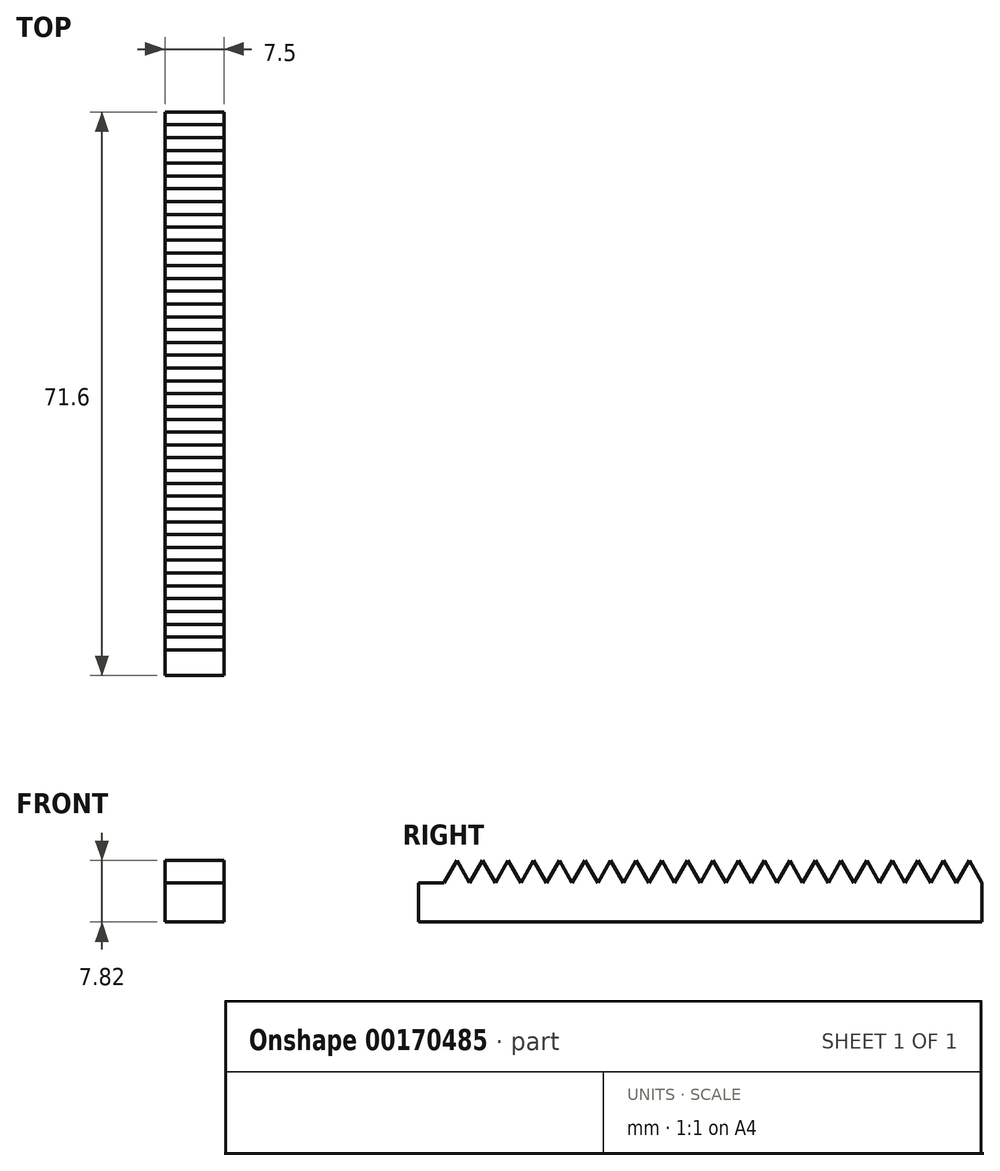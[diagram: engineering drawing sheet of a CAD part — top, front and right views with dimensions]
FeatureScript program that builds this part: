
annotation { "Feature Type Name" : "Feature", "Feature Type Description" : "" }
export const myFeature = defineFeature(function(context is Context, id is Id, definition is map)
    precondition{}
    {
        {
            var Q0;
            Q0=qCreatedBy(makeId("Right.planeOp"),FACE);
            var sketch = newSketch(context, id + "F0", { "sketchPlane" : qUnion([Q0])});
            skLineSegment(sketch, "E0.bottom", {"start": v(35.8, 2.5) * mm, "end": v(-35.8, 2.5) * mm});
            skLineSegment(sketch, "E0.top", {"start": v(35.8, -2.5) * mm, "end": v(-35.8, -2.5) * mm});
            skLineSegment(sketch, "E0.left", {"start": v(35.8, 2.5) * mm, "end": v(35.8, -2.5) * mm});
            skLineSegment(sketch, "E0.right", {"start": v(-35.8, 2.5) * mm, "end": v(-35.8, -2.5) * mm});
            skPoint(sketch, "E0.middle", {"position": v(0, 0) * mm});
            skLineSegment(sketch, "E1", {"start": v(-35.8, 2.5) * mm, "end": v(-32.54, 2.5) * mm});
            skLineSegment(sketch, "E2", {"start": v(-32.54, 2.5) * mm, "end": v(-34.17, 5.32) * mm});
            skLineSegment(sketch, "E3", {"start": v(-34.17, 5.32) * mm, "end": v(-35.8, 2.5) * mm});
            skLineSegment(sketch, "E4.1.0.0", {"start": v(-29.29, 2.5) * mm, "end": v(-30.91, 5.32) * mm});
            skLineSegment(sketch, "E4.1.0.1", {"start": v(-30.91, 5.32) * mm, "end": v(-32.54, 2.5) * mm});
            skLineSegment(sketch, "E4.1.0.2", {"start": v(-32.54, 2.5) * mm, "end": v(-29.29, 2.5) * mm});
            skLineSegment(sketch, "E4.2.0.0", {"start": v(-26.03, 2.5) * mm, "end": v(-27.66, 5.32) * mm});
            skLineSegment(sketch, "E4.2.0.1", {"start": v(-27.66, 5.32) * mm, "end": v(-29.29, 2.5) * mm});
            skLineSegment(sketch, "E4.2.0.2", {"start": v(-29.29, 2.5) * mm, "end": v(-26.03, 2.5) * mm});
            skLineSegment(sketch, "E4.3.0.0", {"start": v(-22.78, 2.5) * mm, "end": v(-24.4, 5.32) * mm});
            skLineSegment(sketch, "E4.3.0.1", {"start": v(-24.4, 5.32) * mm, "end": v(-26.03, 2.5) * mm});
            skLineSegment(sketch, "E4.3.0.2", {"start": v(-26.03, 2.5) * mm, "end": v(-22.78, 2.5) * mm});
            skLineSegment(sketch, "E4.4.0.0", {"start": v(-19.52, 2.5) * mm, "end": v(-21.15, 5.32) * mm});
            skLineSegment(sketch, "E4.4.0.1", {"start": v(-21.15, 5.32) * mm, "end": v(-22.78, 2.5) * mm});
            skLineSegment(sketch, "E4.4.0.2", {"start": v(-22.78, 2.5) * mm, "end": v(-19.52, 2.5) * mm});
            skLineSegment(sketch, "E4.5.0.0", {"start": v(-16.27, 2.5) * mm, "end": v(-17.9, 5.32) * mm});
            skLineSegment(sketch, "E4.5.0.1", {"start": v(-17.9, 5.32) * mm, "end": v(-19.52, 2.5) * mm});
            skLineSegment(sketch, "E4.5.0.2", {"start": v(-19.52, 2.5) * mm, "end": v(-16.27, 2.5) * mm});
            skLineSegment(sketch, "E4.6.0.0", {"start": v(-13.02, 2.5) * mm, "end": v(-14.64, 5.32) * mm});
            skLineSegment(sketch, "E4.6.0.1", {"start": v(-14.64, 5.32) * mm, "end": v(-16.27, 2.5) * mm});
            skLineSegment(sketch, "E4.6.0.2", {"start": v(-16.27, 2.5) * mm, "end": v(-13.02, 2.5) * mm});
            skLineSegment(sketch, "E4.7.0.0", {"start": v(-9.76, 2.5) * mm, "end": v(-11.39, 5.32) * mm});
            skLineSegment(sketch, "E4.7.0.1", {"start": v(-11.39, 5.32) * mm, "end": v(-13.02, 2.5) * mm});
            skLineSegment(sketch, "E4.7.0.2", {"start": v(-13.02, 2.5) * mm, "end": v(-9.76, 2.5) * mm});
            skLineSegment(sketch, "E4.8.0.0", {"start": v(-6.5, 2.5) * mm, "end": v(-8.14, 5.32) * mm});
            skLineSegment(sketch, "E4.8.0.1", {"start": v(-8.14, 5.32) * mm, "end": v(-9.76, 2.5) * mm});
            skLineSegment(sketch, "E4.8.0.2", {"start": v(-9.76, 2.5) * mm, "end": v(-6.5, 2.5) * mm});
            skLineSegment(sketch, "E4.9.0.0", {"start": v(-3.25, 2.5) * mm, "end": v(-4.88, 5.32) * mm});
            skLineSegment(sketch, "E4.9.0.1", {"start": v(-4.88, 5.32) * mm, "end": v(-6.5, 2.5) * mm});
            skLineSegment(sketch, "E4.9.0.2", {"start": v(-6.5, 2.5) * mm, "end": v(-3.25, 2.5) * mm});
            skLineSegment(sketch, "E4.10.0.0", {"start": v(0, 2.5) * mm, "end": v(-1.63, 5.32) * mm});
            skLineSegment(sketch, "E4.10.0.1", {"start": v(-1.63, 5.32) * mm, "end": v(-3.25, 2.5) * mm});
            skLineSegment(sketch, "E4.10.0.2", {"start": v(-3.25, 2.5) * mm, "end": v(0, 2.5) * mm});
            skLineSegment(sketch, "E4.11.0.0", {"start": v(3.25, 2.5) * mm, "end": v(1.63, 5.32) * mm});
            skLineSegment(sketch, "E4.11.0.1", {"start": v(1.63, 5.32) * mm, "end": v(0, 2.5) * mm});
            skLineSegment(sketch, "E4.11.0.2", {"start": v(0, 2.5) * mm, "end": v(3.25, 2.5) * mm});
            skLineSegment(sketch, "E4.12.0.0", {"start": v(6.5, 2.5) * mm, "end": v(4.88, 5.32) * mm});
            skLineSegment(sketch, "E4.12.0.1", {"start": v(4.88, 5.32) * mm, "end": v(3.25, 2.5) * mm});
            skLineSegment(sketch, "E4.12.0.2", {"start": v(3.25, 2.5) * mm, "end": v(6.5, 2.5) * mm});
            skLineSegment(sketch, "E4.13.0.0", {"start": v(9.76, 2.5) * mm, "end": v(8.14, 5.32) * mm});
            skLineSegment(sketch, "E4.13.0.1", {"start": v(8.14, 5.32) * mm, "end": v(6.5, 2.5) * mm});
            skLineSegment(sketch, "E4.13.0.2", {"start": v(6.5, 2.5) * mm, "end": v(9.76, 2.5) * mm});
            skLineSegment(sketch, "E4.14.0.0", {"start": v(13.02, 2.5) * mm, "end": v(11.39, 5.32) * mm});
            skLineSegment(sketch, "E4.14.0.1", {"start": v(11.39, 5.32) * mm, "end": v(9.76, 2.5) * mm});
            skLineSegment(sketch, "E4.14.0.2", {"start": v(9.76, 2.5) * mm, "end": v(13.02, 2.5) * mm});
            skLineSegment(sketch, "E4.15.0.0", {"start": v(16.27, 2.5) * mm, "end": v(14.64, 5.32) * mm});
            skLineSegment(sketch, "E4.15.0.1", {"start": v(14.64, 5.32) * mm, "end": v(13.02, 2.5) * mm});
            skLineSegment(sketch, "E4.15.0.2", {"start": v(13.02, 2.5) * mm, "end": v(16.27, 2.5) * mm});
            skLineSegment(sketch, "E4.16.0.0", {"start": v(19.52, 2.5) * mm, "end": v(17.9, 5.32) * mm});
            skLineSegment(sketch, "E4.16.0.1", {"start": v(17.9, 5.32) * mm, "end": v(16.27, 2.5) * mm});
            skLineSegment(sketch, "E4.16.0.2", {"start": v(16.27, 2.5) * mm, "end": v(19.52, 2.5) * mm});
            skLineSegment(sketch, "E4.17.0.0", {"start": v(22.78, 2.5) * mm, "end": v(21.15, 5.32) * mm});
            skLineSegment(sketch, "E4.17.0.1", {"start": v(21.15, 5.32) * mm, "end": v(19.52, 2.5) * mm});
            skLineSegment(sketch, "E4.17.0.2", {"start": v(19.52, 2.5) * mm, "end": v(22.78, 2.5) * mm});
            skLineSegment(sketch, "E4.18.0.0", {"start": v(26.03, 2.5) * mm, "end": v(24.4, 5.32) * mm});
            skLineSegment(sketch, "E4.18.0.1", {"start": v(24.4, 5.32) * mm, "end": v(22.78, 2.5) * mm});
            skLineSegment(sketch, "E4.18.0.2", {"start": v(22.78, 2.5) * mm, "end": v(26.03, 2.5) * mm});
            skLineSegment(sketch, "E4.19.0.0", {"start": v(29.29, 2.5) * mm, "end": v(27.66, 5.32) * mm});
            skLineSegment(sketch, "E4.19.0.1", {"start": v(27.66, 5.32) * mm, "end": v(26.03, 2.5) * mm});
            skLineSegment(sketch, "E4.19.0.2", {"start": v(26.03, 2.5) * mm, "end": v(29.29, 2.5) * mm});
            skLineSegment(sketch, "E4.20.0.0", {"start": v(32.54, 2.5) * mm, "end": v(30.91, 5.32) * mm});
            skLineSegment(sketch, "E4.20.0.1", {"start": v(30.91, 5.32) * mm, "end": v(29.29, 2.5) * mm});
            skLineSegment(sketch, "E4.20.0.2", {"start": v(29.29, 2.5) * mm, "end": v(32.54, 2.5) * mm});
            skLineSegment(sketch, "E4.21.0.0", {"start": v(35.8, 2.5) * mm, "end": v(34.17, 5.32) * mm});
            skLineSegment(sketch, "E4.21.0.1", {"start": v(34.17, 5.32) * mm, "end": v(32.54, 2.5) * mm});
            skLineSegment(sketch, "E4.21.0.2", {"start": v(32.54, 2.5) * mm, "end": v(35.8, 2.5) * mm});
            skLineSegment(sketch, "E4.direction1", {"start": v(-35.8, 2.5) * mm, "end": v(-32.54, 2.5) * mm, "construction": true});
            skSolve(sketch);
        }
        {
            var Q0;
            Q0=makeQuery(id+"F0.imprint","IMPRINT",FACE,{"disambiguationData":[TD([[makeQuery(id+"F0.imprint","IMPRINT",EDGE,{"derivedFrom":sQuery(id+"F0.wireOp",EDGE,"E0.top")}),-1.0]])]});
            var Q1;
            Q1=makeQuery(id+"F0.imprint","IMPRINT",FACE,{"disambiguationData":[TD([[makeQuery(id+"F0.imprint","IMPRINT",EDGE,{"derivedFrom":sQuery(id+"F0.wireOp",EDGE,"E4.19.0.0")}),1.0]])]});
            var Q2;
            Q2=makeQuery(id+"F0.imprint","IMPRINT",FACE,{"disambiguationData":[TD([[makeQuery(id+"F0.imprint","IMPRINT",EDGE,{"derivedFrom":sQuery(id+"F0.wireOp",EDGE,"E4.20.0.0")}),1.0]])]});
            var Q3;
            Q3=makeQuery(id+"F0.imprint","IMPRINT",FACE,{"disambiguationData":[TD([[makeQuery(id+"F0.imprint","IMPRINT",EDGE,{"derivedFrom":sQuery(id+"F0.wireOp",EDGE,"E4.21.0.0")}),1.0]])]});
            var Q4;
            Q4=makeQuery(id+"F0.imprint","IMPRINT",FACE,{"disambiguationData":[TD([[makeQuery(id+"F0.imprint","IMPRINT",EDGE,{"derivedFrom":sQuery(id+"F0.wireOp",EDGE,"E4.15.0.0")}),1.0]])]});
            var Q5;
            Q5=makeQuery(id+"F0.imprint","IMPRINT",FACE,{"disambiguationData":[TD([[makeQuery(id+"F0.imprint","IMPRINT",EDGE,{"derivedFrom":sQuery(id+"F0.wireOp",EDGE,"E4.13.0.0")}),1.0]])]});
            var Q6;
            Q6=makeQuery(id+"F0.imprint","IMPRINT",FACE,{"disambiguationData":[TD([[makeQuery(id+"F0.imprint","IMPRINT",EDGE,{"derivedFrom":sQuery(id+"F0.wireOp",EDGE,"E4.16.0.0")}),1.0]])]});
            var Q7;
            Q7=makeQuery(id+"F0.imprint","IMPRINT",FACE,{"disambiguationData":[TD([[makeQuery(id+"F0.imprint","IMPRINT",EDGE,{"derivedFrom":sQuery(id+"F0.wireOp",EDGE,"E4.14.0.0")}),1.0]])]});
            var Q8;
            Q8=makeQuery(id+"F0.imprint","IMPRINT",FACE,{"disambiguationData":[TD([[makeQuery(id+"F0.imprint","IMPRINT",EDGE,{"derivedFrom":sQuery(id+"F0.wireOp",EDGE,"E1")}),1.0]])]});
            var Q9;
            Q9=makeQuery(id+"F0.imprint","IMPRINT",FACE,{"disambiguationData":[TD([[makeQuery(id+"F0.imprint","IMPRINT",EDGE,{"derivedFrom":sQuery(id+"F0.wireOp",EDGE,"E4.1.0.0")}),1.0]])]});
            var Q10;
            Q10=makeQuery(id+"F0.imprint","IMPRINT",FACE,{"disambiguationData":[TD([[makeQuery(id+"F0.imprint","IMPRINT",EDGE,{"derivedFrom":sQuery(id+"F0.wireOp",EDGE,"E4.2.0.0")}),1.0]])]});
            var Q11;
            Q11=makeQuery(id+"F0.imprint","IMPRINT",FACE,{"disambiguationData":[TD([[makeQuery(id+"F0.imprint","IMPRINT",EDGE,{"derivedFrom":sQuery(id+"F0.wireOp",EDGE,"E4.3.0.0")}),1.0]])]});
            var Q12;
            Q12=makeQuery(id+"F0.imprint","IMPRINT",FACE,{"disambiguationData":[TD([[makeQuery(id+"F0.imprint","IMPRINT",EDGE,{"derivedFrom":sQuery(id+"F0.wireOp",EDGE,"E4.4.0.0")}),1.0]])]});
            var Q13;
            Q13=makeQuery(id+"F0.imprint","IMPRINT",FACE,{"disambiguationData":[TD([[makeQuery(id+"F0.imprint","IMPRINT",EDGE,{"derivedFrom":sQuery(id+"F0.wireOp",EDGE,"E4.5.0.0")}),1.0]])]});
            var Q14;
            Q14=makeQuery(id+"F0.imprint","IMPRINT",FACE,{"disambiguationData":[TD([[makeQuery(id+"F0.imprint","IMPRINT",EDGE,{"derivedFrom":sQuery(id+"F0.wireOp",EDGE,"E4.6.0.0")}),1.0]])]});
            var Q15;
            Q15=makeQuery(id+"F0.imprint","IMPRINT",FACE,{"disambiguationData":[TD([[makeQuery(id+"F0.imprint","IMPRINT",EDGE,{"derivedFrom":sQuery(id+"F0.wireOp",EDGE,"E4.7.0.0")}),1.0]])]});
            var Q16;
            Q16=makeQuery(id+"F0.imprint","IMPRINT",FACE,{"disambiguationData":[TD([[makeQuery(id+"F0.imprint","IMPRINT",EDGE,{"derivedFrom":sQuery(id+"F0.wireOp",EDGE,"E4.8.0.0")}),1.0]])]});
            var Q17;
            Q17=makeQuery(id+"F0.imprint","IMPRINT",FACE,{"disambiguationData":[TD([[makeQuery(id+"F0.imprint","IMPRINT",EDGE,{"derivedFrom":sQuery(id+"F0.wireOp",EDGE,"E4.9.0.0")}),1.0]])]});
            var Q18;
            Q18=makeQuery(id+"F0.imprint","IMPRINT",FACE,{"disambiguationData":[TD([[makeQuery(id+"F0.imprint","IMPRINT",EDGE,{"derivedFrom":sQuery(id+"F0.wireOp",EDGE,"E4.10.0.0")}),1.0]])]});
            var Q19;
            Q19=makeQuery(id+"F0.imprint","IMPRINT",FACE,{"disambiguationData":[TD([[makeQuery(id+"F0.imprint","IMPRINT",EDGE,{"derivedFrom":sQuery(id+"F0.wireOp",EDGE,"E4.11.0.0")}),1.0]])]});
            var Q20;
            Q20=makeQuery(id+"F0.imprint","IMPRINT",FACE,{"disambiguationData":[TD([[makeQuery(id+"F0.imprint","IMPRINT",EDGE,{"derivedFrom":sQuery(id+"F0.wireOp",EDGE,"E4.12.0.0")}),1.0]])]});
            var Q21;
            Q21=makeQuery(id+"F0.imprint","IMPRINT",FACE,{"disambiguationData":[TD([[makeQuery(id+"F0.imprint","IMPRINT",EDGE,{"derivedFrom":sQuery(id+"F0.wireOp",EDGE,"E4.17.0.0")}),1.0]])]});
            var Q22;
            Q22=makeQuery(id+"F0.imprint","IMPRINT",FACE,{"disambiguationData":[TD([[makeQuery(id+"F0.imprint","IMPRINT",EDGE,{"derivedFrom":sQuery(id+"F0.wireOp",EDGE,"E4.18.0.0")}),1.0]])]});
            extrude(context, id + "F1", {"entities" : qUnion([Q0, Q1, Q2, Q3, Q4, Q5, Q6, Q7, Q8, Q9, Q10, Q11, Q12, Q13, Q14, Q15, Q16, Q17, Q18, Q19, Q20, Q21, Q22]), "endBound" : BoundingType.SYMMETRIC, "depth" : 7.5 * mm});
        }
    });
